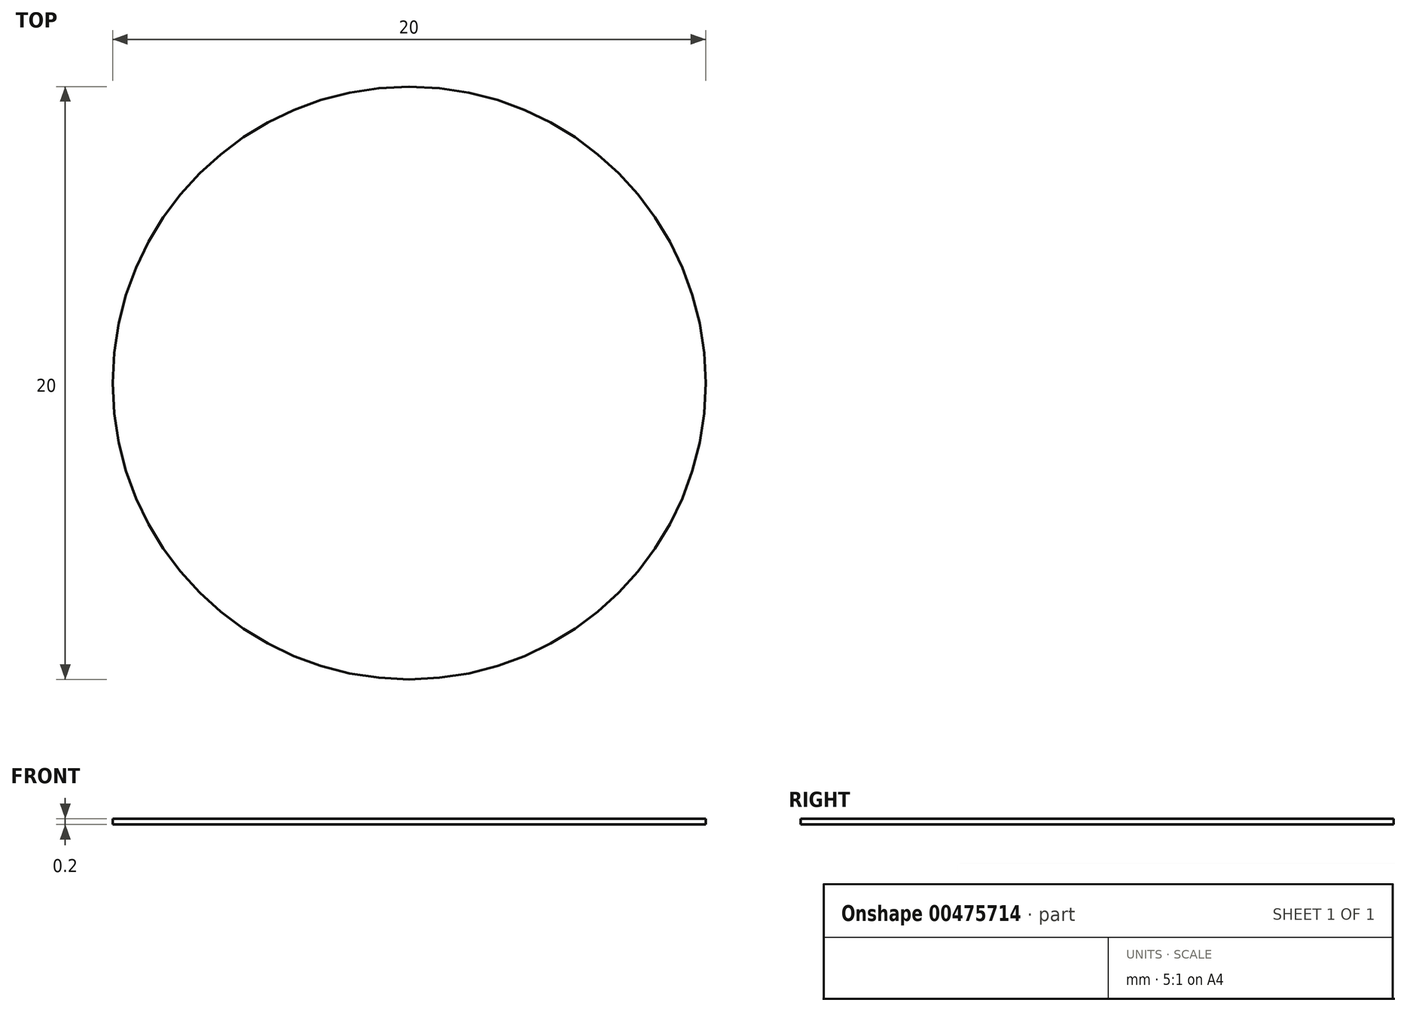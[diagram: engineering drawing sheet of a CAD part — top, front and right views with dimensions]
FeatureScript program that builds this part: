
annotation { "Feature Type Name" : "Feature", "Feature Type Description" : "" }
export const myFeature = defineFeature(function(context is Context, id is Id, definition is map)
    precondition{}
    {
        {
            var Q0;
            Q0=qCreatedBy(makeId("Top.planeOp"),FACE);
            var sketch = newSketch(context, id + "F0", { "sketchPlane" : qUnion([Q0])});
            skCircle(sketch, "E0", {"center": v(0, 0) * mm, "radius": 10 * mm});
            skSolve(sketch);
        }
        {
            var Q0;
            Q0=makeQuery(id+"F0.imprint","IMPRINT",FACE,{"disambiguationData":[TD([[makeQuery(id+"F0.imprint","IMPRINT",EDGE,{"derivedFrom":sQuery(id+"F0.wireOp",EDGE,"E0")}),1.0]])]});
            extrude(context, id + "F1", {"entities" : qUnion([Q0]), "offsetDistance" : 25 * mm, "depth" : 0.2 * mm});
        }
    });
